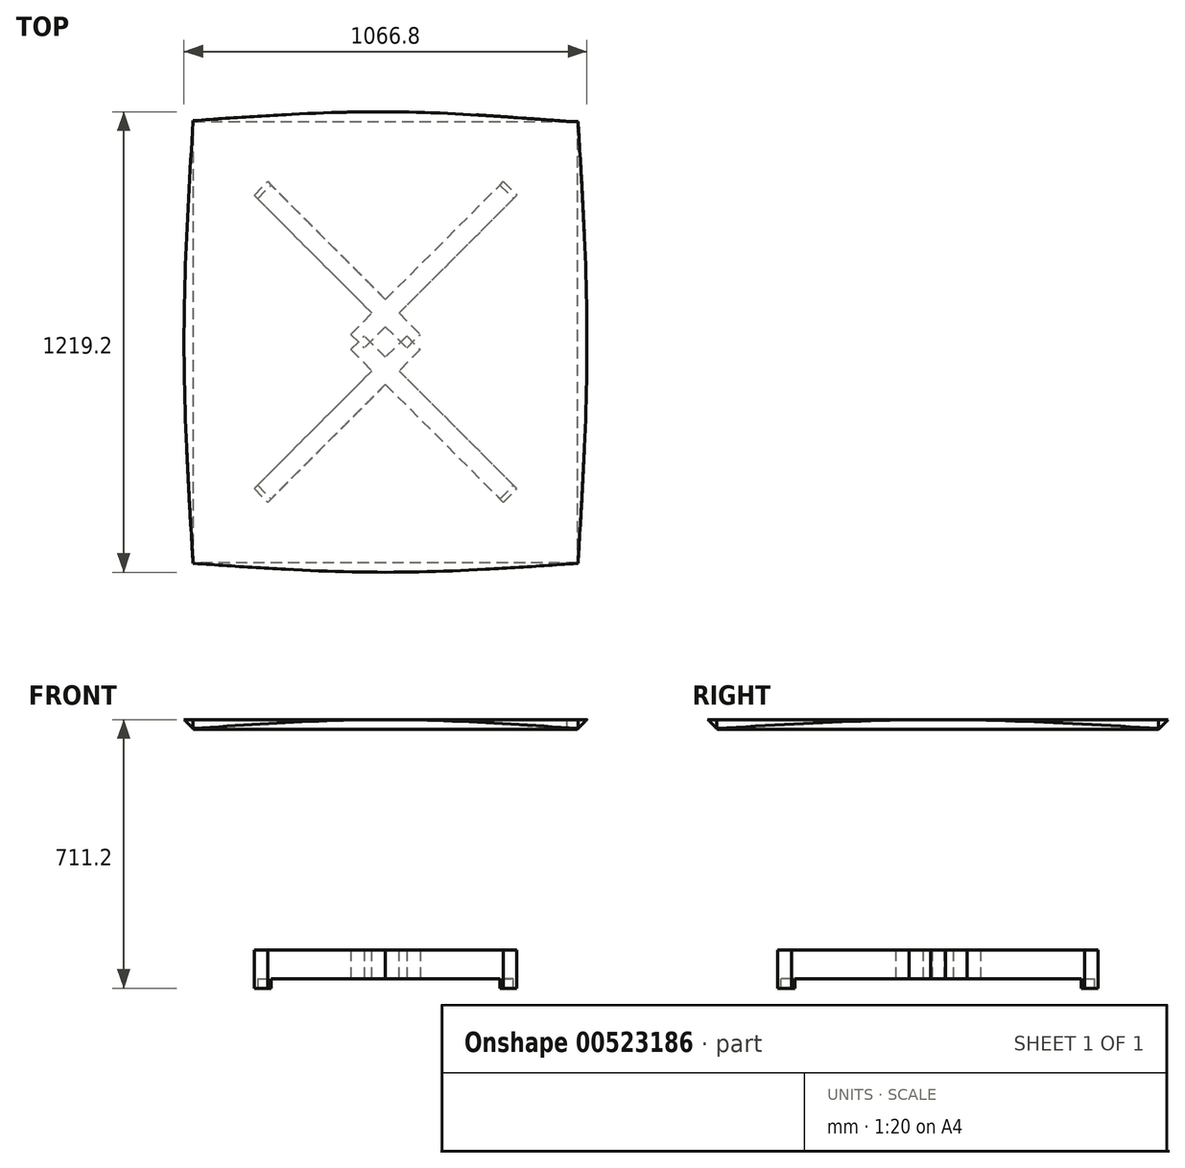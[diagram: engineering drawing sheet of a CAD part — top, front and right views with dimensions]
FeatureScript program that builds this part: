
annotation { "Feature Type Name" : "Feature", "Feature Type Description" : "" }
export const myFeature = defineFeature(function(context is Context, id is Id, definition is map)
    precondition{}
    {
        {
            var Q0;
            Q0=qCreatedBy(makeId("Top.planeOp"),FACE);
            var sketch = newSketch(context, id + "F0", { "sketchPlane" : qUnion([Q0])});
            skLineSegment(sketch, "E0.bottom", {"start": v(-533.4, 609.6) * mm, "end": v(533.4, 609.6) * mm});
            skLineSegment(sketch, "E0.top", {"start": v(-533.4, -609.6) * mm, "end": v(533.4, -609.6) * mm});
            skLineSegment(sketch, "E0.left", {"start": v(-533.4, 609.6) * mm, "end": v(-533.4, -609.6) * mm});
            skLineSegment(sketch, "E0.right", {"start": v(533.4, 609.6) * mm, "end": v(533.4, -609.6) * mm});
            skPoint(sketch, "E1.visualSharp", {"position": v(-533.4, 609.6) * mm});
            skPoint(sketch, "E2.visualSharp", {"position": v(533.4, 609.6) * mm});
            skPoint(sketch, "E3.visualSharp", {"position": v(533.4, -609.6) * mm});
            skPoint(sketch, "E4.visualSharp", {"position": v(-533.4, -609.6) * mm});
            skSolve(sketch);
        }
        {
            var Q0;
            Q0=makeQuery(id+"F0.imprint","IMPRINT",FACE,{"disambiguationData":[TD([[makeQuery(id+"F0.imprint","IMPRINT",EDGE,{"derivedFrom":sQuery(id+"F0.wireOp",EDGE,"E0.bottom")}),-1.0]])]});
            extrude(context, id + "F1", {"entities" : qUnion([Q0]), "depth" : 25.4 * mm, "offsetDistance" : 25.4 * mm});
        }
        {
            var Q0;
            Q0=makeQuery(id+"F1.opExtrude","CAP_EDGE",EDGE,{"disambiguationData":[OSD([sQuery(id+"F0.wireOp",EDGE,"E0.right")])],"isStart":true});
            var Q1;
            Q1=makeQuery(id+"F1.opExtrude","CAP_EDGE",EDGE,{"disambiguationData":[OSD([sQuery(id+"F0.wireOp",EDGE,"E0.top")])],"isStart":true});
            var Q2;
            Q2=makeQuery(id+"F1.opExtrude","CAP_EDGE",EDGE,{"disambiguationData":[OSD([sQuery(id+"F0.wireOp",EDGE,"E0.left")])],"isStart":true});
            var Q3;
            Q3=makeQuery(id+"F1.opExtrude","CAP_EDGE",EDGE,{"disambiguationData":[OSD([sQuery(id+"F0.wireOp",EDGE,"E0.bottom")])],"isStart":true});
            chamfer(context, id + "F2", {"entities" : qUnion([Q0, Q1, Q2, Q3]), "width" : 25.4 * mm, "tangentPropagation" : true});
        }
        {
            var Q0;
            Q0=makeQuery(id+"F1.opExtrude","CAP_FACE",FACE,{"disambiguationData":[OSD([sQuery(id+"F0.wireOp",EDGE,"E0.bottom"),sQuery(id+"F0.wireOp",EDGE,"E0.top"),sQuery(id+"F0.wireOp",EDGE,"E0.left"),sQuery(id+"F0.wireOp",EDGE,"E0.right")])],"isStart":false});
            var sketch = newSketch(context, id + "F3", { "sketchPlane" : qUnion([Q0])});
            skLineSegment(sketch, "E5.0", {"start": v(-533.4, -584.2) * mm, "end": v(533.4, -584.2) * mm});
            skLineSegment(sketch, "E5.1", {"start": v(508, 609.6) * mm, "end": v(508, -609.6) * mm});
            skLineSegment(sketch, "E6.0", {"start": v(-533.4, 584.2) * mm, "end": v(533.4, 584.2) * mm});
            skLineSegment(sketch, "E6.1", {"start": v(-508, 609.6) * mm, "end": v(-508, -609.6) * mm});
            skLineSegment(sketch, "E7.0", {"start": v(-533.4, -609.6) * mm, "end": v(533.4, -609.6) * mm});
            skLineSegment(sketch, "E8.0", {"start": v(-533.4, 609.6) * mm, "end": v(-533.4, -609.6) * mm});
            skLineSegment(sketch, "E9.0", {"start": v(-533.4, 609.6) * mm, "end": v(533.4, 609.6) * mm});
            skLineSegment(sketch, "E10.0", {"start": v(533.4, 609.6) * mm, "end": v(533.4, -609.6) * mm});
            skFitSpline(sketch, "E11", {"points": [v(508, -609.6) * mm, v(533.4, 0) * mm, v(508, 609.6) * mm], "startDerivative": vector(76.2, 1219.2) * mm, "endDerivative": vector(-76.2, 1219.2) * mm});
            skFitSpline(sketch, "E12", {"points": [v(-508, -609.6) * mm, v(-533.4, 0) * mm, v(-508, 609.6) * mm], "startDerivative": vector(-76.2, 1219.2) * mm, "endDerivative": vector(76.2, 1219.2) * mm});
            skFitSpline(sketch, "E13", {"points": [v(-533.4, -584.2) * mm, v(0, -609.6) * mm, v(533.4, -584.2) * mm], "startDerivative": vector(1066.8, -76.2) * mm, "endDerivative": vector(1066.8, 76.2) * mm});
            skFitSpline(sketch, "E14", {"points": [v(-533.4, 584.2) * mm, v(0, 609.6) * mm, v(480.85, 584.2) * mm], "startDerivative": vector(1066.8, 76.2) * mm, "endDerivative": vector(1066.8, -76.2) * mm});
            skSolve(sketch);
        }
        {
            var Q0;
            {var subQ0=sQuery(id+"F3.wireOp",EDGE,"E7.0");var subQ3=sQuery(id+"F3.wireOp",EDGE,"E13");var subQ5=makeQuery(id+"F3.imprint","INTERSECT",VERTEX,{"derivedFrom":[subQ0,subQ3]});Q0=makeQuery(id+"F3.imprint","IMPRINT",FACE,{"disambiguationData":[TD([[makeQuery(id+"F3.imprint","IMPRINT",EDGE,{"disambiguationData":[TD([[subQ5,1.0]])],"derivedFrom":subQ3}),-1.0]])]});}
            var Q1;
            {var subQ0=sQuery(id+"F3.wireOp",EDGE,"E8.0");var subQ1=sQuery(id+"F3.wireOp",EDGE,"E7.0");var subQ2=makeQuery(id+"F3.imprint","INTERSECT",VERTEX,{"derivedFrom":[subQ1,subQ0]});Q1=makeQuery(id+"F3.imprint","IMPRINT",FACE,{"disambiguationData":[TD([[makeQuery(id+"F3.imprint","IMPRINT",EDGE,{"disambiguationData":[TD([[subQ2,-1.0]])],"derivedFrom":subQ1}),1.0]])]});}
            var Q2;
            {var subQ0=sQuery(id+"F3.wireOp",EDGE,"E8.0");var subQ3=sQuery(id+"F3.wireOp",EDGE,"E12");var subQ5=makeQuery(id+"F3.imprint","INTERSECT",VERTEX,{"derivedFrom":[subQ0,subQ3]});Q2=makeQuery(id+"F3.imprint","IMPRINT",FACE,{"disambiguationData":[TD([[makeQuery(id+"F3.imprint","IMPRINT",EDGE,{"disambiguationData":[TD([[subQ5,1.0]])],"derivedFrom":subQ3}),1.0]])]});}
            var Q3;
            {var subQ0=sQuery(id+"F3.wireOp",EDGE,"E8.0");var subQ3=sQuery(id+"F3.wireOp",EDGE,"E12");var subQ5=makeQuery(id+"F3.imprint","INTERSECT",VERTEX,{"derivedFrom":[subQ0,subQ3]});Q3=makeQuery(id+"F3.imprint","IMPRINT",FACE,{"disambiguationData":[TD([[makeQuery(id+"F3.imprint","IMPRINT",EDGE,{"disambiguationData":[TD([[subQ5,-1.0]])],"derivedFrom":subQ3}),1.0]])]});}
            var Q4;
            {var subQ0=sQuery(id+"F3.wireOp",EDGE,"E9.0");var subQ1=sQuery(id+"F3.wireOp",EDGE,"E8.0");var subQ2=makeQuery(id+"F3.imprint","INTERSECT",VERTEX,{"derivedFrom":[subQ1,subQ0]});Q4=makeQuery(id+"F3.imprint","IMPRINT",FACE,{"disambiguationData":[TD([[makeQuery(id+"F3.imprint","IMPRINT",EDGE,{"disambiguationData":[TD([[subQ2,-1.0]])],"derivedFrom":subQ1}),1.0]])]});}
            var Q5;
            {var subQ0=sQuery(id+"F3.wireOp",EDGE,"E9.0");var subQ3=sQuery(id+"F3.wireOp",EDGE,"E14");var subQ5=makeQuery(id+"F3.imprint","INTERSECT",VERTEX,{"derivedFrom":[subQ0,subQ3]});Q5=makeQuery(id+"F3.imprint","IMPRINT",FACE,{"disambiguationData":[TD([[makeQuery(id+"F3.imprint","IMPRINT",EDGE,{"disambiguationData":[TD([[subQ5,1.0]])],"derivedFrom":subQ3}),1.0]])]});}
            var Q6;
            {var subQ0=sQuery(id+"F3.wireOp",EDGE,"E9.0");var subQ3=sQuery(id+"F3.wireOp",EDGE,"E14");var subQ5=makeQuery(id+"F3.imprint","INTERSECT",VERTEX,{"derivedFrom":[subQ0,subQ3]});Q6=makeQuery(id+"F3.imprint","IMPRINT",FACE,{"disambiguationData":[TD([[makeQuery(id+"F3.imprint","IMPRINT",EDGE,{"disambiguationData":[TD([[subQ5,-1.0]])],"derivedFrom":subQ3}),1.0]])]});}
            var Q7;
            {var subQ0=sQuery(id+"F3.wireOp",EDGE,"E10.0");var subQ1=sQuery(id+"F3.wireOp",EDGE,"E9.0");var subQ2=makeQuery(id+"F3.imprint","INTERSECT",VERTEX,{"derivedFrom":[subQ1,subQ0]});Q7=makeQuery(id+"F3.imprint","IMPRINT",FACE,{"disambiguationData":[TD([[makeQuery(id+"F3.imprint","IMPRINT",EDGE,{"disambiguationData":[TD([[subQ2,1.0]])],"derivedFrom":subQ1}),-1.0]])]});}
            var Q8;
            {var subQ0=sQuery(id+"F3.wireOp",EDGE,"E10.0");var subQ3=sQuery(id+"F3.wireOp",EDGE,"E11");var subQ5=makeQuery(id+"F3.imprint","INTERSECT",VERTEX,{"derivedFrom":[subQ0,subQ3]});Q8=makeQuery(id+"F3.imprint","IMPRINT",FACE,{"disambiguationData":[TD([[makeQuery(id+"F3.imprint","IMPRINT",EDGE,{"disambiguationData":[TD([[subQ5,-1.0]])],"derivedFrom":subQ3}),-1.0]])]});}
            var Q9;
            {var subQ0=sQuery(id+"F3.wireOp",EDGE,"E10.0");var subQ3=sQuery(id+"F3.wireOp",EDGE,"E11");var subQ5=makeQuery(id+"F3.imprint","INTERSECT",VERTEX,{"derivedFrom":[subQ0,subQ3]});Q9=makeQuery(id+"F3.imprint","IMPRINT",FACE,{"disambiguationData":[TD([[makeQuery(id+"F3.imprint","IMPRINT",EDGE,{"disambiguationData":[TD([[subQ5,1.0]])],"derivedFrom":subQ3}),-1.0]])]});}
            var Q10;
            {var subQ0=sQuery(id+"F3.wireOp",EDGE,"E10.0");var subQ1=sQuery(id+"F3.wireOp",EDGE,"E7.0");var subQ2=makeQuery(id+"F3.imprint","INTERSECT",VERTEX,{"derivedFrom":[subQ1,subQ0]});Q10=makeQuery(id+"F3.imprint","IMPRINT",FACE,{"disambiguationData":[TD([[makeQuery(id+"F3.imprint","IMPRINT",EDGE,{"disambiguationData":[TD([[subQ2,1.0]])],"derivedFrom":subQ1}),1.0]])]});}
            var Q11;
            {var subQ0=sQuery(id+"F3.wireOp",EDGE,"E7.0");var subQ3=sQuery(id+"F3.wireOp",EDGE,"E13");var subQ5=makeQuery(id+"F3.imprint","INTERSECT",VERTEX,{"derivedFrom":[subQ0,subQ3]});Q11=makeQuery(id+"F3.imprint","IMPRINT",FACE,{"disambiguationData":[TD([[makeQuery(id+"F3.imprint","IMPRINT",EDGE,{"disambiguationData":[TD([[subQ5,-1.0]])],"derivedFrom":subQ3}),-1.0]])]});}
            var Q12;
            {var subQ1=sQuery(id+"F3.wireOp",EDGE,"E6.0");var subQ3=sQuery(id+"F3.wireOp",EDGE,"E11");var subQ4=makeQuery(id+"F3.imprint","INTERSECT",VERTEX,{"derivedFrom":[subQ1,subQ3]});Q12=makeQuery(id+"F3.imprint","IMPRINT",FACE,{"disambiguationData":[TD([[makeQuery(id+"F3.imprint","IMPRINT",EDGE,{"disambiguationData":[TD([[subQ4,-1.0]])],"derivedFrom":subQ3}),-1.0]])]});}
            var Q13;
            {var subQ1=sQuery(id+"F3.wireOp",EDGE,"E5.1");var subQ3=sQuery(id+"F3.wireOp",EDGE,"E14");var subQ4=makeQuery(id+"F3.imprint","INTERSECT",VERTEX,{"derivedFrom":[subQ1,subQ3]});Q13=makeQuery(id+"F3.imprint","IMPRINT",FACE,{"disambiguationData":[TD([[makeQuery(id+"F3.imprint","IMPRINT",EDGE,{"disambiguationData":[TD([[subQ4,-1.0]])],"derivedFrom":subQ3}),1.0]])]});}
            var Q14;
            {var subQ1=sQuery(id+"F3.wireOp",EDGE,"E5.0");var subQ3=sQuery(id+"F3.wireOp",EDGE,"E11");var subQ4=makeQuery(id+"F3.imprint","INTERSECT",VERTEX,{"derivedFrom":[subQ1,subQ3]});Q14=makeQuery(id+"F3.imprint","IMPRINT",FACE,{"disambiguationData":[TD([[makeQuery(id+"F3.imprint","IMPRINT",EDGE,{"disambiguationData":[TD([[subQ4,1.0]])],"derivedFrom":subQ3}),-1.0]])]});}
            var Q15;
            {var subQ1=sQuery(id+"F3.wireOp",EDGE,"E5.1");var subQ3=sQuery(id+"F3.wireOp",EDGE,"E13");var subQ4=makeQuery(id+"F3.imprint","INTERSECT",VERTEX,{"derivedFrom":[subQ1,subQ3]});Q15=makeQuery(id+"F3.imprint","IMPRINT",FACE,{"disambiguationData":[TD([[makeQuery(id+"F3.imprint","IMPRINT",EDGE,{"disambiguationData":[TD([[subQ4,-1.0]])],"derivedFrom":subQ3}),-1.0]])]});}
            var Q16;
            {var subQ1=sQuery(id+"F3.wireOp",EDGE,"E5.0");var subQ3=sQuery(id+"F3.wireOp",EDGE,"E12");var subQ4=makeQuery(id+"F3.imprint","INTERSECT",VERTEX,{"derivedFrom":[subQ1,subQ3]});Q16=makeQuery(id+"F3.imprint","IMPRINT",FACE,{"disambiguationData":[TD([[makeQuery(id+"F3.imprint","IMPRINT",EDGE,{"disambiguationData":[TD([[subQ4,1.0]])],"derivedFrom":subQ3}),1.0]])]});}
            var Q17;
            {var subQ1=sQuery(id+"F3.wireOp",EDGE,"E6.1");var subQ3=sQuery(id+"F3.wireOp",EDGE,"E13");var subQ4=makeQuery(id+"F3.imprint","INTERSECT",VERTEX,{"derivedFrom":[subQ1,subQ3]});Q17=makeQuery(id+"F3.imprint","IMPRINT",FACE,{"disambiguationData":[TD([[makeQuery(id+"F3.imprint","IMPRINT",EDGE,{"disambiguationData":[TD([[subQ4,1.0]])],"derivedFrom":subQ3}),-1.0]])]});}
            var Q18;
            {var subQ1=sQuery(id+"F3.wireOp",EDGE,"E6.1");var subQ3=sQuery(id+"F3.wireOp",EDGE,"E14");var subQ4=makeQuery(id+"F3.imprint","INTERSECT",VERTEX,{"derivedFrom":[subQ1,subQ3]});Q18=makeQuery(id+"F3.imprint","IMPRINT",FACE,{"disambiguationData":[TD([[makeQuery(id+"F3.imprint","IMPRINT",EDGE,{"disambiguationData":[TD([[subQ4,1.0]])],"derivedFrom":subQ3}),1.0]])]});}
            var Q19;
            {var subQ1=sQuery(id+"F3.wireOp",EDGE,"E6.0");var subQ3=sQuery(id+"F3.wireOp",EDGE,"E12");var subQ4=makeQuery(id+"F3.imprint","INTERSECT",VERTEX,{"derivedFrom":[subQ1,subQ3]});Q19=makeQuery(id+"F3.imprint","IMPRINT",FACE,{"disambiguationData":[TD([[makeQuery(id+"F3.imprint","IMPRINT",EDGE,{"disambiguationData":[TD([[subQ4,-1.0]])],"derivedFrom":subQ3}),1.0]])]});}
            var Q20;
            {var subQ1=sQuery(id+"F3.wireOp",EDGE,"E5.1");var subQ3=sQuery(id+"F3.wireOp",EDGE,"E6.0");var subQ4=makeQuery(id+"F3.imprint","INTERSECT",VERTEX,{"derivedFrom":[subQ1,subQ3]});Q20=makeQuery(id+"F3.imprint","IMPRINT",FACE,{"disambiguationData":[TD([[makeQuery(id+"F3.imprint","IMPRINT",EDGE,{"disambiguationData":[TD([[subQ4,-1.0]])],"derivedFrom":subQ3}),1.0]])]});}
            extrude(context, id + "F4", {"entities" : qUnion([Q0, Q1, Q2, Q3, Q4, Q5, Q6, Q7, Q8, Q9, Q10, Q11, Q12, Q13, Q14, Q15, Q16, Q17, Q18, Q19, Q20]), "operationType" : NewBodyOperationType.REMOVE, "oppositeDirection" : true, "depth" : 25.4 * mm, "offsetDistance" : 25.4 * mm});
        }
        {
            var Q0;
            Q0=makeQuery(id+"F1.opExtrude","CAP_FACE",FACE,{"disambiguationData":[OSD([sQuery(id+"F0.wireOp",EDGE,"E0.bottom"),sQuery(id+"F0.wireOp",EDGE,"E0.top"),sQuery(id+"F0.wireOp",EDGE,"E0.left"),sQuery(id+"F0.wireOp",EDGE,"E0.right")])],"isStart":false});
            cPlane(context, id + "F5", {"entities" : qUnion([Q0]), "cplaneType" : CPlaneType.OFFSET, "offset" : 711.2 * mm, "oppositeDirection" : true, "width" : 152.4 * mm, "height" : 152.4 * mm});
        }
        {
            var Q0;
            Q0=qCreatedBy(id+"F5.planeOp",FACE);
            var sketch = newSketch(context, id + "F6", { "sketchPlane" : qUnion([Q0])});
            skFitSpline(sketch, "E15.0.0", {"points": [v(-533.4, -584.2) * mm, v(-355.6, -596.9) * mm, v(0, -622.3) * mm, v(355.6, -596.9) * mm, v(533.4, -584.2) * mm]});
            skFitSpline(sketch, "E15.0.1", {"points": [v(508, -609.6) * mm, v(520.7, -406.4) * mm, v(546.1, 0) * mm, v(520.7, 406.4) * mm, v(508, 609.6) * mm]});
            skFitSpline(sketch, "E15.0.2", {"points": [v(508, -609.6) * mm, v(520.7, -406.4) * mm, v(546.1, 0) * mm, v(520.7, 406.4) * mm, v(508, 609.6) * mm]});
            skLineSegment(sketch, "E15.0.3", {"start": v(509.59, 584.2) * mm, "end": v(480.85, 584.2) * mm});
            skFitSpline(sketch, "E15.0.4", {"points": [v(480.85, 584.2) * mm, v(307.65, 596.57) * mm, v(4.66, 622.33) * mm, v(-351, 597.23) * mm, v(-533.4, 584.2) * mm]});
            skLineSegment(sketch, "E15.0.5", {"start": v(0, 609.6) * mm, "end": v(-19.42, 609.6) * mm});
            skFitSpline(sketch, "E15.0.6", {"points": [v(480.85, 584.2) * mm, v(307.65, 596.57) * mm, v(4.66, 622.33) * mm, v(-351, 597.23) * mm, v(-533.4, 584.2) * mm]});
            skFitSpline(sketch, "E15.0.7", {"points": [v(-508, 609.6) * mm, v(-520.7, 406.4) * mm, v(-546.1, 0) * mm, v(-520.7, -406.4) * mm, v(-508, -609.6) * mm]});
            skFitSpline(sketch, "E15.0.8", {"points": [v(-508, 609.6) * mm, v(-520.7, 406.4) * mm, v(-546.1, 0) * mm, v(-520.7, -406.4) * mm, v(-508, -609.6) * mm]});
            skFitSpline(sketch, "E15.0.9", {"points": [v(-533.4, -584.2) * mm, v(-355.6, -596.9) * mm, v(0, -622.3) * mm, v(355.6, -596.9) * mm, v(533.4, -584.2) * mm]});
            skLineSegment(sketch, "E16", {"start": v(-311.91, -424.26) * mm, "end": v(92.2, -20.15) * mm});
            skLineSegment(sketch, "E17", {"start": v(-92.2, -20.15) * mm, "end": v(311.91, -424.26) * mm});
            skLineSegment(sketch, "E18", {"start": v(311.91, -424.26) * mm, "end": v(347.84, -388.34) * mm});
            skLineSegment(sketch, "E19", {"start": v(347.84, -388.34) * mm, "end": v(-56.28, 15.77) * mm});
            skLineSegment(sketch, "E20", {"start": v(-56.28, 15.77) * mm, "end": v(-92.2, -20.15) * mm});
            skLineSegment(sketch, "E21", {"start": v(92.2, -20.15) * mm, "end": v(56.28, 15.77) * mm});
            skLineSegment(sketch, "E22", {"start": v(56.28, 15.77) * mm, "end": v(-347.84, -388.34) * mm});
            skLineSegment(sketch, "E23", {"start": v(-347.84, -388.34) * mm, "end": v(-311.91, -424.26) * mm});
            skLineSegment(sketch, "E24", {"start": v(0, 0) * mm, "end": v(0, -609.6) * mm, "construction": true});
            skLineSegment(sketch, "E25", {"start": v(0, -76.43) * mm, "end": v(509.48, -585.9) * mm, "construction": true});
            skLineSegment(sketch, "E26", {"start": v(0, -76.43) * mm, "end": v(-509.48, -585.9) * mm, "construction": true});
            skSolve(sketch);
        }
        {
            var Q0;
            {var subQ0=sQuery(id+"F6.wireOp",EDGE,"E23");Q0=makeQuery(id+"F6.imprint","IMPRINT",FACE,{"disambiguationData":[TD([[makeQuery(id+"F6.imprint","IMPRINT",EDGE,{"derivedFrom":subQ0}),1.0]])]});}
            var Q1;
            {var subQ0=sQuery(id+"F6.wireOp",EDGE,"E17");var subQ1=sQuery(id+"F6.wireOp",EDGE,"E16");var subQ2=makeQuery(id+"F6.imprint","INTERSECT",VERTEX,{"derivedFrom":[subQ1,subQ0]});Q1=makeQuery(id+"F6.imprint","IMPRINT",FACE,{"disambiguationData":[TD([[makeQuery(id+"F6.imprint","IMPRINT",EDGE,{"disambiguationData":[TD([[subQ2,-1.0]])],"derivedFrom":subQ1}),1.0]])]});}
            var Q2;
            {var subQ0=sQuery(id+"F6.wireOp",EDGE,"E21");Q2=makeQuery(id+"F6.imprint","IMPRINT",FACE,{"disambiguationData":[TD([[makeQuery(id+"F6.imprint","IMPRINT",EDGE,{"derivedFrom":subQ0}),1.0]])]});}
            extrude(context, id + "F7", {"entities" : qUnion([Q0, Q1, Q2]), "depth" : 101.6 * mm, "offsetDistance" : 25.4 * mm});
        }
        {
            var Q0;
            Q0=makeQuery(id+"F7.opExtrude","SWEPT_FACE",FACE,{"disambiguationData":[OSD([sQuery(id+"F6.wireOp",EDGE,"E16")])]});
            var sketch = newSketch(context, id + "F8", { "sketchPlane" : qUnion([Q0])});
            skPoint(sketch, "E27.oppositeSnap0", {"position": v(-79.44, -660.4) * mm});
            skLineSegment(sketch, "E27.bottom", {"start": v(50.94, -685.8) * mm, "end": v(-507.86, -685.8) * mm});
            skLineSegment(sketch, "E27.top", {"start": v(50.94, -660.4) * mm, "end": v(-507.86, -660.4) * mm});
            skLineSegment(sketch, "E27.left", {"start": v(50.94, -685.8) * mm, "end": v(50.94, -660.4) * mm});
            skLineSegment(sketch, "E27.right", {"start": v(-507.86, -685.8) * mm, "end": v(-507.86, -660.4) * mm});
            skSolve(sketch);
        }
        {
            var Q0;
            Q0=makeQuery(id+"F8.imprint","IMPRINT",FACE,{"disambiguationData":[TD([[makeQuery(id+"F8.imprint","IMPRINT",EDGE,{"derivedFrom":sQuery(id+"F8.wireOp",EDGE,"E27.bottom")}),1.0]])]});
            extrude(context, id + "F9", {"entities" : qUnion([Q0]), "operationType" : NewBodyOperationType.REMOVE, "endBound" : BoundingType.UP_TO_NEXT, "oppositeDirection" : true, "depth" : 25.4 * mm, "offsetDistance" : 25.4 * mm});
        }
        {
            var Q0;
            {var subQ0=sQuery(id+"F6.wireOp",EDGE,"E20");Q0=makeQuery(id+"F6.imprint","IMPRINT",FACE,{"disambiguationData":[TD([[makeQuery(id+"F6.imprint","IMPRINT",EDGE,{"derivedFrom":subQ0}),1.0]])]});}
            var Q1;
            {var subQ0=sQuery(id+"F6.wireOp",EDGE,"E17");var subQ1=sQuery(id+"F6.wireOp",EDGE,"E16");var subQ2=makeQuery(id+"F6.imprint","INTERSECT",VERTEX,{"derivedFrom":[subQ1,subQ0]});Q1=makeQuery(id+"F6.imprint","IMPRINT",FACE,{"disambiguationData":[TD([[makeQuery(id+"F6.imprint","IMPRINT",EDGE,{"disambiguationData":[TD([[subQ2,-1.0]])],"derivedFrom":subQ1}),1.0]])]});}
            var Q2;
            {var subQ5=sQuery(id+"F6.wireOp",EDGE,"E18");Q2=makeQuery(id+"F6.imprint","IMPRINT",FACE,{"disambiguationData":[TD([[makeQuery(id+"F6.imprint","IMPRINT",EDGE,{"derivedFrom":subQ5}),1.0]])]});}
            extrude(context, id + "F10", {"entities" : qUnion([Q0, Q1, Q2]), "operationType" : NewBodyOperationType.ADD, "depth" : 101.6 * mm, "offsetDistance" : 25.4 * mm});
        }
        {
            var Q0;
            Q0=makeQuery(id+"F10.opExtrude","SWEPT_FACE",FACE,{"disambiguationData":[OSD([sQuery(id+"F6.wireOp",EDGE,"E19")])]});
            var sketch = newSketch(context, id + "F11", { "sketchPlane" : qUnion([Q0])});
            skLineSegment(sketch, "E28.bottom", {"start": v(-507.86, -685.8) * mm, "end": v(50.94, -685.8) * mm});
            skLineSegment(sketch, "E28.top", {"start": v(-507.86, -660.4) * mm, "end": v(50.94, -660.4) * mm});
            skLineSegment(sketch, "E28.left", {"start": v(-507.86, -685.8) * mm, "end": v(-507.86, -660.4) * mm});
            skLineSegment(sketch, "E28.right", {"start": v(50.94, -685.8) * mm, "end": v(50.94, -660.4) * mm});
            skSolve(sketch);
        }
        {
            var Q0;
            Q0=makeQuery(id+"F11.imprint","IMPRINT",FACE,{"disambiguationData":[TD([[makeQuery(id+"F11.imprint","IMPRINT",EDGE,{"derivedFrom":sQuery(id+"F11.wireOp",EDGE,"E28.bottom")}),1.0]])]});
            extrude(context, id + "F12", {"entities" : qUnion([Q0]), "operationType" : NewBodyOperationType.REMOVE, "endBound" : BoundingType.UP_TO_NEXT, "oppositeDirection" : true, "depth" : 25.4 * mm, "offsetDistance" : 25.4 * mm});
        }
        {
            var Q0;
            Q0=makeQuery(id+"F7.opExtrude","SWEPT_BODY",BODY,{"disambiguationData":[OSD([sQuery(id+"F6.wireOp",EDGE,"E16"),sQuery(id+"F6.wireOp",EDGE,"E17"),sQuery(id+"F6.wireOp",EDGE,"E18"),sQuery(id+"F6.wireOp",EDGE,"E19"),sQuery(id+"F6.wireOp",EDGE,"E20"),sQuery(id+"F6.wireOp",EDGE,"E21"),sQuery(id+"F6.wireOp",EDGE,"E22"),sQuery(id+"F6.wireOp",EDGE,"E23")])]});
            var Q1;
            Q1=qCreatedBy(makeId("Front.planeOp"),FACE);
            mirror(context, id + "F13", {"operationType" : NewBodyOperationType.ADD, "entities" : qUnion([Q0]), "mirrorPlane" : qUnion([Q1])});
        }
    });
